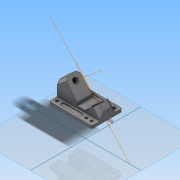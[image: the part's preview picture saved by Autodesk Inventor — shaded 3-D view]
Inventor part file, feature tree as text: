
AUTODESK INVENTOR PART (.ipt)
format: ipt  version: 2014 (Build 180170000, 170)  size: 360,960 bytes
history: native  units: in
note: dims shown in document units (in); Inventor stores cm internally (conversion verified against a paired STEP export)
features: sketch x15, extrude x13, projected_geometry x9, plane x3, chamfer x3, other x3, mirror x1, draft x1, fillet x1
ambient origin geometry x8: Origin, YZ Plane, XZ Plane, XY Plane, X Axis, Y Axis, Z Axis, Center Point
bodies: Solid1 (feature_tree)
feature tree (49):
  extrude  "Extrusion1"  Depth=2.2in
  plane  "Work Plane1"
  extrude  "Extrusion2"  Depth=0.21in TaperAngle=0.0deg
  extrude  "Extrusion3"  Depth=0.205in
  mirror  "Mirror1"
  extrude  "Extrusion4"  Depth=0.278in
  extrude  "Extrusion5"  Depth=0.302in
  extrude  "Extrusion6"  Depth=0.21in TaperAngle=0.0deg
  chamfer  "Chamfer1"  Distance=0.05in
  extrude  "Extrusion7"  Depth=0.57in
  chamfer  "Chamfer2"  Distance=0.15in
  other  "Work Axis1"
  extrude  "Extrusion8"  Depth=1.06in TaperAngle=0.0deg
  extrude  "Extrusion9"  Depth=0.75in
  chamfer  "Chamfer3"  Distance=0.75in
  extrude  "Extrusion10"  Depth=0.25in
  draft  "FaceDraft5"
  extrude  "Extrusion11"  Depth=0.5in TaperAngle=0.0deg
  sketch  "Sketch14"  dims[d26=1.06in d27=0.65in d28=0.0in]
  sketch  "Sketch15"  dims[d34=0.3436in d35=0.3436in d36=0.75in d37=0.0in]
  extrude  "Extrusion13"  Depth=0.25in TaperAngle=45.0deg
  fillet  "Fillet2"  Radius=1.46in
  other  "Work Axis2"
  extrude  "Extrusion14"  Depth=0.03in TaperAngle=0.0deg
  plane  "Work Plane4"
  sketch  "Sketch18"  dims[d42=0.5in d43=0.5in d44=0.0in d46=0.25in d47=0.125in d48=45.0deg d49=1.46in d50=1.3in d51=0.0in d52=0.2in d53=0.3436in d54=0.3436in d55=1.3in d56=0.0in d57=0.2in d58=0.125in d59=45.0deg d63=0.66in d64=0.125in d65=0.4in d66=0.0in d67=0.3436in d68=0.37in d69=0.4in d70=0.0in d71=1.1in d72=0.76in d73=0.0in d74=0.11in d75=0.8in d76=0.8933in d77=90.0deg d78=0.4in d79=0.4in d82=0.76in d83=0.0in d84=0.135in d85=1.08in d86=0.75in d87=0.05in d88=0.05in d89=0.5in d90=0.03in d91=0.0in d92=0.0137in d93=0.8125in d94=2.125in]
  other  "Work Axis3"
  sketch  "Sketch1"  dims[d0=3.08in d1=2.2in]
  sketch  "Sketch2"  dims[d2=0.1in d3=0.21in d4=0.0in]
  sketch  "Sketch3"  dims[d5=0.205in d6=0.205in]
  plane  "Work Plane2"
  sketch  "Sketch4"  dims[d7=0.205in d8=0.278in]
  projected_geometry  "Projected Loop1"
  sketch  "Sketch5"  dims[d9=0.2875in d11=0.302in]
  projected_geometry  "Projected Loop2"
  sketch  "Sketch8"  dims[d13=0.375in d14=0.21in d15=0.0in]
  projected_geometry  "Projected Loop4"
  sketch  "Sketch9"  dims[d16=0.3in]
  sketch  "Sketch10"  dims[d17=0.45in]
  projected_geometry  "Projected Loop5"
  sketch  "Sketch11"  dims[d18=0.45in]
  projected_geometry  "Projected Loop6"
  sketch  "Sketch12"  dims[d19=0.0in d20=0.05in d21=0.0in]
  projected_geometry  "Projected Loop7"
  sketch  "Sketch13"  dims[d22=0.57in d23=0.57in d24=0.15in d25=0.0in]
  projected_geometry  "Projected Loop8"
  projected_geometry  "Projected Loop9"
  projected_geometry  "Projected Loop10"
  sketch  "Sketch17"  dims[d38=0.25in d39=0.125in d40=45.0deg d41=0.7in]
